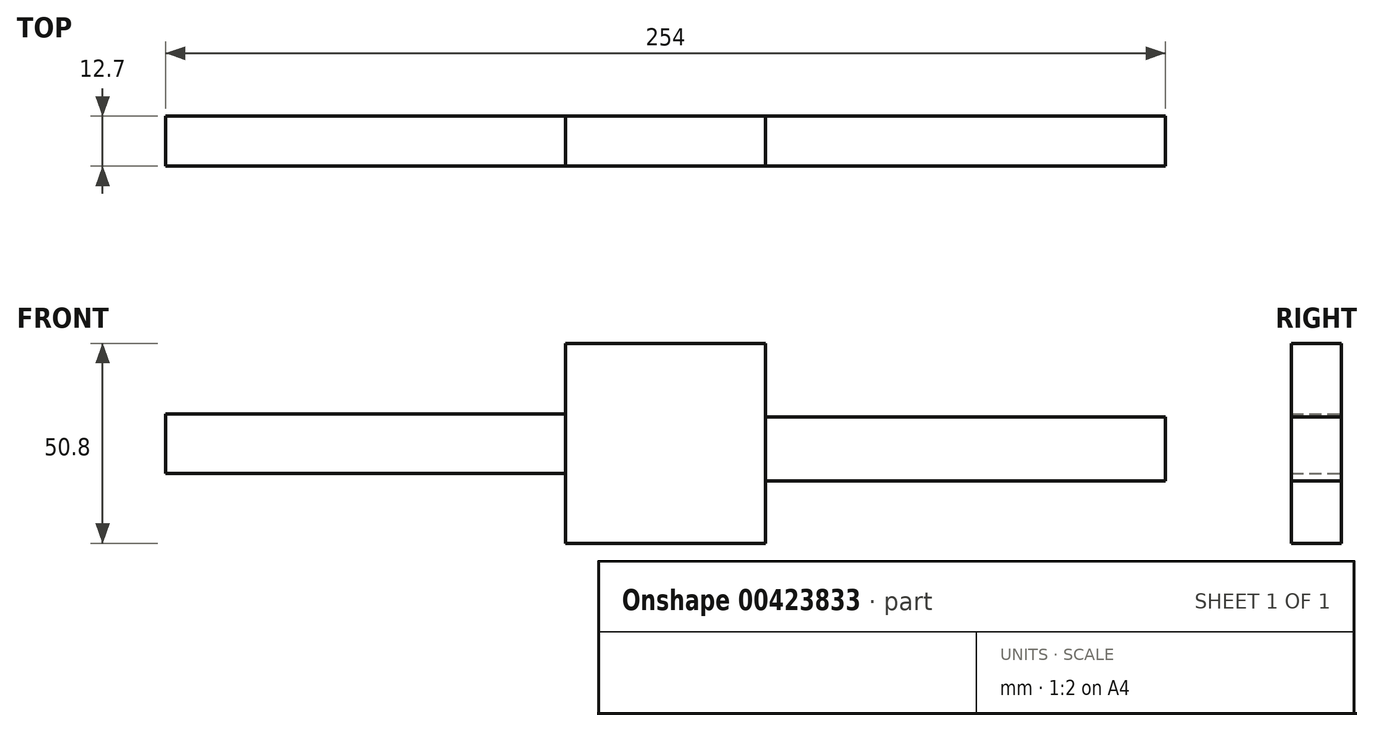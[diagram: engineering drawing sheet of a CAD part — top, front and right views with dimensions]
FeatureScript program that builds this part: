
annotation { "Feature Type Name" : "Feature", "Feature Type Description" : "" }
export const myFeature = defineFeature(function(context is Context, id is Id, definition is map)
    precondition{}
    {
        {
            var Q0;
            Q0=qCreatedBy(makeId("Front.planeOp"),FACE);
            var sketch = newSketch(context, id + "F0", { "sketchPlane" : qUnion([Q0])});
            skLineSegment(sketch, "E0.bottom", {"start": v(-25.4, 25.4) * mm, "end": v(25.4, 25.4) * mm});
            skLineSegment(sketch, "E0.top", {"start": v(-25.4, -25.4) * mm, "end": v(25.4, -25.4) * mm});
            skLineSegment(sketch, "E0.left", {"start": v(-25.4, 25.4) * mm, "end": v(-25.4, -25.4) * mm});
            skLineSegment(sketch, "E0.right", {"start": v(25.4, 25.4) * mm, "end": v(25.4, -25.4) * mm});
            skPoint(sketch, "E0.middle", {"position": v(0, 0) * mm});
            skSolve(sketch);
        }
        {
            var Q0;
            Q0=makeQuery(id+"F0.imprint","IMPRINT",FACE,{"disambiguationData":[TD([[makeQuery(id+"F0.imprint","IMPRINT",EDGE,{"derivedFrom":sQuery(id+"F0.wireOp",EDGE,"E0.bottom")}),-1.0]])]});
            extrude(context, id + "F1", {"entities" : qUnion([Q0]), "depth" : 12.7 * mm});
        }
        {
            var Q0;
            Q0=makeQuery(id+"F1.opExtrude","SWEPT_FACE",FACE,{"disambiguationData":[OSD([sQuery(id+"F0.wireOp",EDGE,"E0.left")])]});
            var sketch = newSketch(context, id + "F2", { "sketchPlane" : qUnion([Q0])});
            skLineSegment(sketch, "E1.bottom", {"start": v(12.7, 7.42) * mm, "end": v(0, 7.42) * mm});
            skLineSegment(sketch, "E1.top", {"start": v(12.7, -7.66) * mm, "end": v(0, -7.66) * mm});
            skLineSegment(sketch, "E1.left", {"start": v(12.7, 7.42) * mm, "end": v(12.7, -7.66) * mm});
            skLineSegment(sketch, "E1.right", {"start": v(0, 7.42) * mm, "end": v(0, -7.66) * mm});
            skSolve(sketch);
        }
        {
            var Q0;
            Q0 = qSketchRegion(id + "F2", true);
            extrude(context, id + "F3", {"entities" : qUnion([Q0]), "depth" : 101.6 * mm});
        }
        {
            var Q0;
            Q0=makeQuery(id+"F1.opExtrude","SWEPT_FACE",FACE,{"disambiguationData":[OSD([sQuery(id+"F0.wireOp",EDGE,"E0.right")])]});
            var sketch = newSketch(context, id + "F4", { "sketchPlane" : qUnion([Q0])});
            skLineSegment(sketch, "E2.bottom", {"start": v(-12.7, 6.76) * mm, "end": v(0, 6.76) * mm});
            skLineSegment(sketch, "E2.top", {"start": v(-12.7, -9.52) * mm, "end": v(0, -9.52) * mm});
            skLineSegment(sketch, "E2.left", {"start": v(-12.7, 6.76) * mm, "end": v(-12.7, -9.52) * mm});
            skLineSegment(sketch, "E2.right", {"start": v(0, 6.76) * mm, "end": v(0, -9.52) * mm});
            skSolve(sketch);
        }
        {
            var Q0;
            Q0=makeQuery(id+"F4.imprint","IMPRINT",FACE,{"disambiguationData":[TD([[makeQuery(id+"F4.imprint","IMPRINT",EDGE,{"derivedFrom":sQuery(id+"F4.wireOp",EDGE,"E2.bottom")}),-1.0]])]});
            extrude(context, id + "F5", {"entities" : qUnion([Q0]), "depth" : 101.6 * mm});
        }
    });
